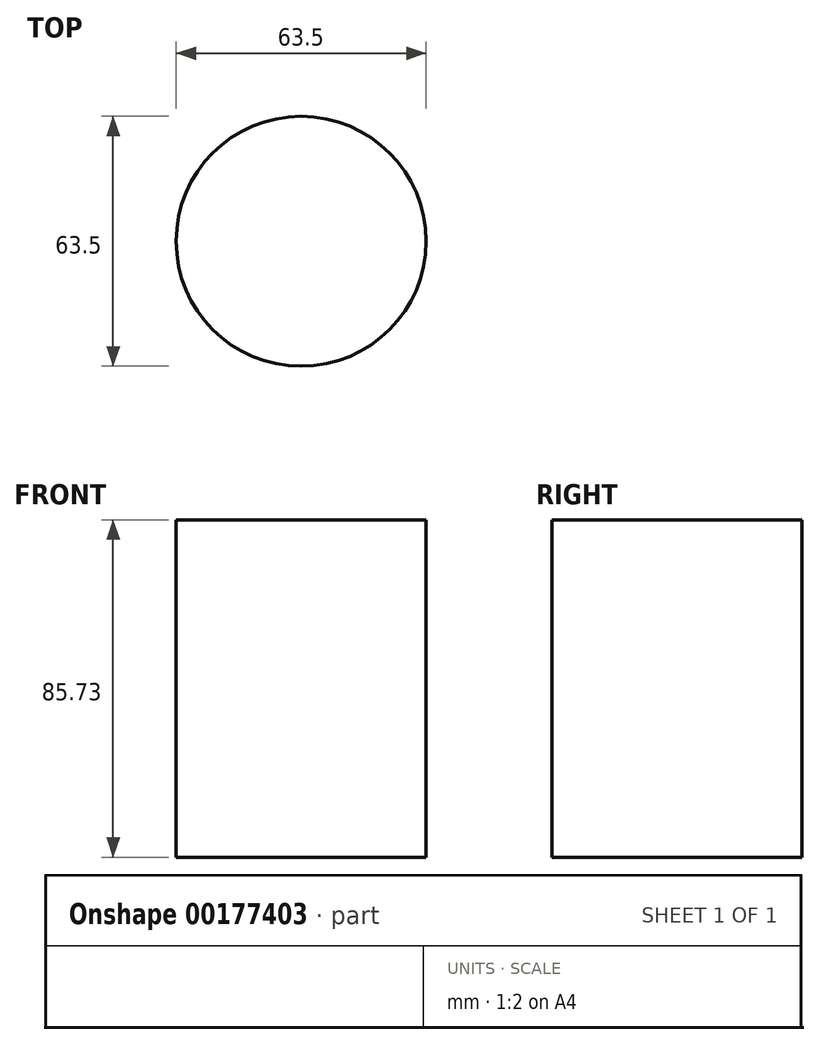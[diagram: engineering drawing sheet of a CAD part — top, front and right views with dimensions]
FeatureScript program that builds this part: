
annotation { "Feature Type Name" : "Feature", "Feature Type Description" : "" }
export const myFeature = defineFeature(function(context is Context, id is Id, definition is map)
    precondition{}
    {
        {
            var Q0;
            Q0=qCreatedBy(makeId("Top.planeOp"),FACE);
            var sketch = newSketch(context, id + "F0", { "sketchPlane" : qUnion([Q0])});
            skCircle(sketch, "E0", {"center": v(0, 0) * mm, "radius": 31.75 * mm});
            skSolve(sketch);
        }
        {
            var Q0;
            Q0=makeQuery(id+"F0.imprint","IMPRINT",FACE,{"disambiguationData":[TD([[makeQuery(id+"F0.imprint","IMPRINT",EDGE,{"derivedFrom":sQuery(id+"F0.wireOp",EDGE,"E0")}),1.0]])]});
            extrude(context, id + "F1", {"entities" : qUnion([Q0]), "depth" : 85.72 * mm});
        }
    });
